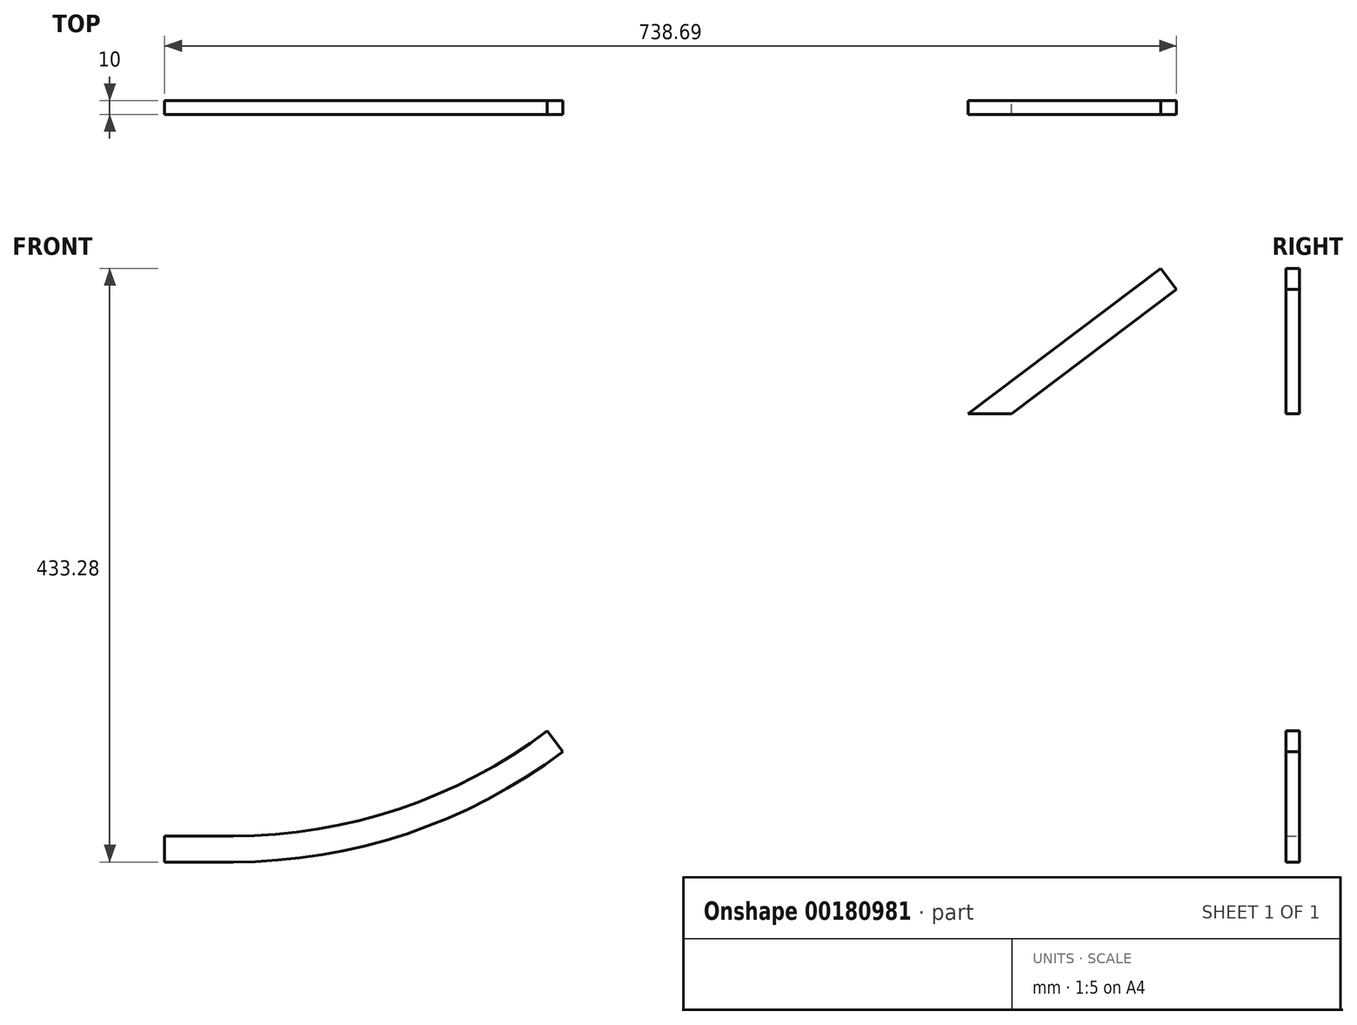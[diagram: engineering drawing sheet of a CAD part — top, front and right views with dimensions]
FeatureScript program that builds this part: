
annotation { "Feature Type Name" : "Feature", "Feature Type Description" : "" }
export const myFeature = defineFeature(function(context is Context, id is Id, definition is map)
    precondition{}
    {
        {
            var Q0;
            Q0=qCreatedBy(makeId("Front.planeOp"),FACE);
            var sketch = newSketch(context, id + "F0", { "sketchPlane" : qUnion([Q0])});
            skLineSegment(sketch, "E0", {"start": v(-52.14, 40.58) * mm, "end": v(412, 390.33) * mm});
            skLineSegment(sketch, "E1", {"start": v(300.31, 122.36) * mm, "end": v(-147.65, -215.2) * mm});
            skLineSegment(sketch, "E2", {"start": v(229, 252.43) * mm, "end": v(229, 16.43) * mm, "construction": true});
            skLineSegment(sketch, "E3", {"start": v(229, 16.43) * mm, "end": v(129, 16.43) * mm});
            skLineSegment(sketch, "E4", {"start": v(129, 16.43) * mm, "end": v(229, 252.43) * mm, "construction": true});
            skCircle(sketch, "E5", {"center": v(129, 16.43) * mm, "radius": 18.5 * mm, "construction": true});
            skLineSegment(sketch, "E6", {"start": v(-376.94, -291.92) * mm, "end": v(-426.94, -291.92) * mm});
            skLineSegment(sketch, "E7", {"start": v(-620.06, -39.97) * mm, "end": v(-292.87, -39.97) * mm});
            skCircle(sketch, "E8", {"center": v(229, 252.43) * mm, "radius": 19 * mm, "construction": true});
            skArc(sketch, "E9.filletArc", {"start": v(-292.87, -39.97) * mm, "mid": v(-165.95, -19.3) * mm, "end": v(-52.14, 40.58) * mm});
            skPoint(sketch, "E10.visualSharp", {"position": v(-262.1, -207.32) * mm});
            skArc(sketch, "E10.filletArc", {"start": v(-376.94, -310.92) * mm, "mid": v(-250.02, -290.25) * mm, "end": v(-136.21, -230.38) * mm});
            skArc(sketch, "E11.0", {"start": v(-376.94, -291.92) * mm, "mid": v(-256.05, -272.23) * mm, "end": v(-147.65, -215.2) * mm});
            skLineSegment(sketch, "E12", {"start": v(311.75, 107.19) * mm, "end": v(300.31, 122.36) * mm});
            skLineSegment(sketch, "E13", {"start": v(423.43, 375.15) * mm, "end": v(412, 390.33) * mm});
            skLineSegment(sketch, "E14", {"start": v(-620.06, -328.6) * mm, "end": v(-620.06, -291.92) * mm});
            skLineSegment(sketch, "E15", {"start": v(-620.06, -74.1) * mm, "end": v(-620.06, -39.97) * mm});
            skLineSegment(sketch, "E16", {"start": v(-620.06, -20.97) * mm, "end": v(-620.06, -39.97) * mm});
            skLineSegment(sketch, "E17", {"start": v(412, 390.33) * mm, "end": v(400.56, 405.5) * mm});
            skLineSegment(sketch, "E18", {"start": v(-620.06, -328.6) * mm, "end": v(-620.06, -347.6) * mm});
            skPoint(sketch, "E19", {"position": v(-342.87, -39.97) * mm});
            skPoint(sketch, "E20", {"position": v(-426.94, -291.92) * mm});
            skLineSegment(sketch, "E21", {"start": v(-292.87, -39.97) * mm, "end": v(-292.87, 360.03) * mm, "construction": true});
            skLineSegment(sketch, "E22", {"start": v(-52.14, 40.58) * mm, "end": v(-292.87, 360.03) * mm, "construction": true});
            skLineSegment(sketch, "E23", {"start": v(-376.94, -310.92) * mm, "end": v(-376.94, 89.08) * mm, "construction": true});
            skLineSegment(sketch, "E24", {"start": v(-136.21, -230.38) * mm, "end": v(-376.94, 89.08) * mm, "construction": true});
            skLineSegment(sketch, "E25.0", {"start": v(311.75, 107.19) * mm, "end": v(-136.21, -230.38) * mm});
            skLineSegment(sketch, "E26", {"start": v(-426.94, -291.92) * mm, "end": v(-426.94, -310.92) * mm});
            skLineSegment(sketch, "E27", {"start": v(-426.94, -310.92) * mm, "end": v(-376.94, -310.92) * mm});
            skPoint(sketch, "E28", {"position": v(-426.94, -310.92) * mm});
            skLineSegment(sketch, "E29", {"start": v(-136.21, -230.38) * mm, "end": v(-147.65, -215.2) * mm});
            skPoint(sketch, "E30", {"position": v(-136.21, -230.38) * mm});
            skPoint(sketch, "E31", {"position": v(-147.65, -215.2) * mm});
            skPoint(sketch, "E32", {"position": v(-52.14, 40.58) * mm});
            skLineSegment(sketch, "E33", {"start": v(-620.06, -328.6) * mm, "end": v(331.46, -328.6) * mm, "construction": true});
            skSolve(sketch);
        }
        {
            var Q0;
            Q0=makeQuery(id+"F0.imprint","IMPRINT",FACE,{"disambiguationData":[TD([[makeQuery(id+"F0.imprint","IMPRINT",EDGE,{"derivedFrom":sQuery(id+"F0.wireOp",EDGE,"E7")}),-1.0]])]});
            var Q1;
            {var subQ4=sQuery(id+"F0.wireOp",EDGE,"E6");Q1=makeQuery(id+"F0.imprint","IMPRINT",FACE,{"disambiguationData":[TD([[makeQuery(id+"F0.imprint","IMPRINT",EDGE,{"derivedFrom":subQ4}),1.0]])]});}
            var Q2;
            {var subQ0=sQuery(id+"F0.wireOp",EDGE,"E12");Q2=makeQuery(id+"F0.imprint","IMPRINT",FACE,{"disambiguationData":[TD([[makeQuery(id+"F0.imprint","IMPRINT",EDGE,{"derivedFrom":subQ0}),1.0]])]});}
            var Q3;
            Q3=makeQuery(id+"F0.imprint","IMPRINT",FACE,{"disambiguationData":[TD([[makeQuery(id+"F0.imprint","IMPRINT",EDGE,{"derivedFrom":sQuery(id+"F0.wireOp",EDGE,"E7")}),1.0]])]});
            var Q4;
            Q4=makeQuery(id+"F0.imprint","IMPRINT",FACE,{"disambiguationData":[TD([[makeQuery(id+"F0.imprint","IMPRINT",EDGE,{"derivedFrom":sQuery(id+"F0.wireOp",EDGE,"mJCDIQvB-bTuc-BmIJ-Bw5x-ThK0byKj1E5t")}),1.0]])]});
            var Q5;
            {var subQ5=sQuery(id+"F0.wireOp",EDGE,"7GOcipid-rF3P-W6yx-JIUi-E45m6GLPwH35");Q5=makeQuery(id+"F0.imprint","IMPRINT",FACE,{"disambiguationData":[TD([[makeQuery(id+"F0.imprint","IMPRINT",EDGE,{"derivedFrom":subQ5}),-1.0]])]});}
            var Q6;
            Q6=makeQuery(id+"F0.imprint","IMPRINT",FACE,{"disambiguationData":[TD([[makeQuery(id+"F0.imprint","IMPRINT",EDGE,{"derivedFrom":sQuery(id+"F0.wireOp",EDGE,"E13")}),-1.0]])]});
            extrude(context, id + "F1", {"entities" : qUnion([Q0, Q1, Q2, Q3, Q4, Q5, Q6]), "depth" : 10 * mm});
        }
    });
